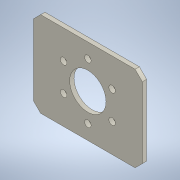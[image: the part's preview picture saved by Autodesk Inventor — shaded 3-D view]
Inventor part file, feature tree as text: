
AUTODESK INVENTOR PART (.ipt)
format: ipt  version: 2022 (Build 260153000, 153)  size: 149,504 bytes
history: native  units: mm
features: other x2, sketch x2, sheet_metal_op x1, hole x1, pattern_circular x1
ambient origin geometry x8: Origin, YZ Plane, XZ Plane, XY Plane, X Axis, Y Axis, Z Axis, Center Point
bodies: Solid1 (feature_tree)
feature tree (7):
  sheet_metal_op  "Face1"
  hole  "Hole1"  [1 undecoded]
  pattern_circular  "Circular Pattern1"  Count=2  [1 undecoded]
  other  "Corner Chamfer1"
  sketch  "Sketch1"  dims[d0=60.0mm d1=47.0mm d2=20.0mm]
  other  "Plate1"
  sketch  "Sketch2"  dims[d3=2.3622mm d4=30.83mm d5=3.6mm d6=6.0mm d7=6.3mm d8=2.0mm d9=90.0deg d10=2.3622mm d11=20.594885mm d12=30.0mm d13=360.0deg d15=4.0mm d16=6.0mm d17=45.0deg]
note: 2 required parameter values undecoded (feature->parameter linkage not recoverable at this tier; creation-order binding heuristic only, values carry confidence <= 0.55)
